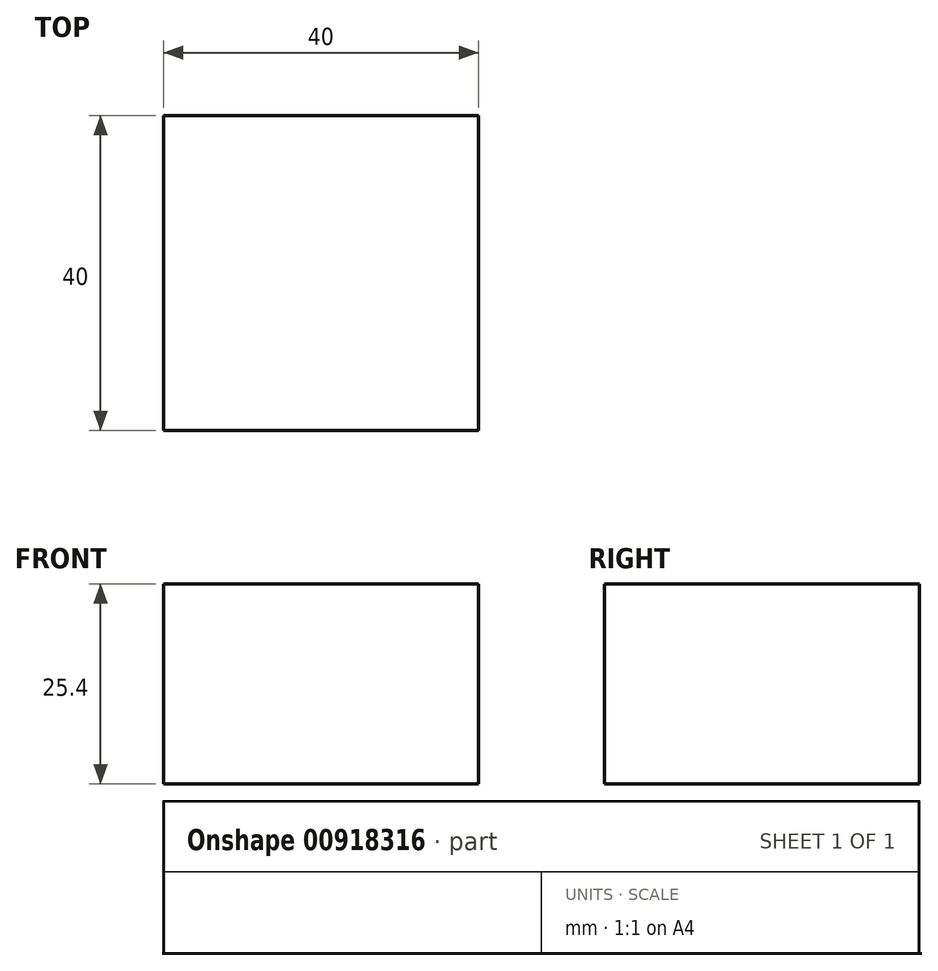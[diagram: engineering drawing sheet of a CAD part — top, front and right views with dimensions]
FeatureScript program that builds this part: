
annotation { "Feature Type Name" : "Feature", "Feature Type Description" : "" }
export const myFeature = defineFeature(function(context is Context, id is Id, definition is map)
    precondition{}
    {
        {
            var Q0;
            Q0=qCreatedBy(makeId("Top.planeOp"),FACE);
            var sketch = newSketch(context, id + "F0", { "sketchPlane" : qUnion([Q0])});
            skLineSegment(sketch, "E0.bottom", {"start": v(-9.35, 24.36) * mm, "end": v(30.65, 24.36) * mm});
            skLineSegment(sketch, "E0.top", {"start": v(-9.35, -15.64) * mm, "end": v(30.65, -15.64) * mm});
            skLineSegment(sketch, "E0.left", {"start": v(-9.35, 24.36) * mm, "end": v(-9.35, -15.64) * mm});
            skLineSegment(sketch, "E0.right", {"start": v(30.65, 24.36) * mm, "end": v(30.65, -15.64) * mm});
            skSolve(sketch);
        }
        {
            var Q0;
            Q0=makeQuery(id+"F0.imprint","IMPRINT",FACE,{"disambiguationData":[TD([[makeQuery(id+"F0.imprint","IMPRINT",EDGE,{"derivedFrom":sQuery(id+"F0.wireOp",EDGE,"E0.bottom")}),-1.0]])]});
            extrude(context, id + "F1", {"entities" : qUnion([Q0]), "depth" : 25.4 * mm, "offsetDistance" : 25.4 * mm});
        }
    });
